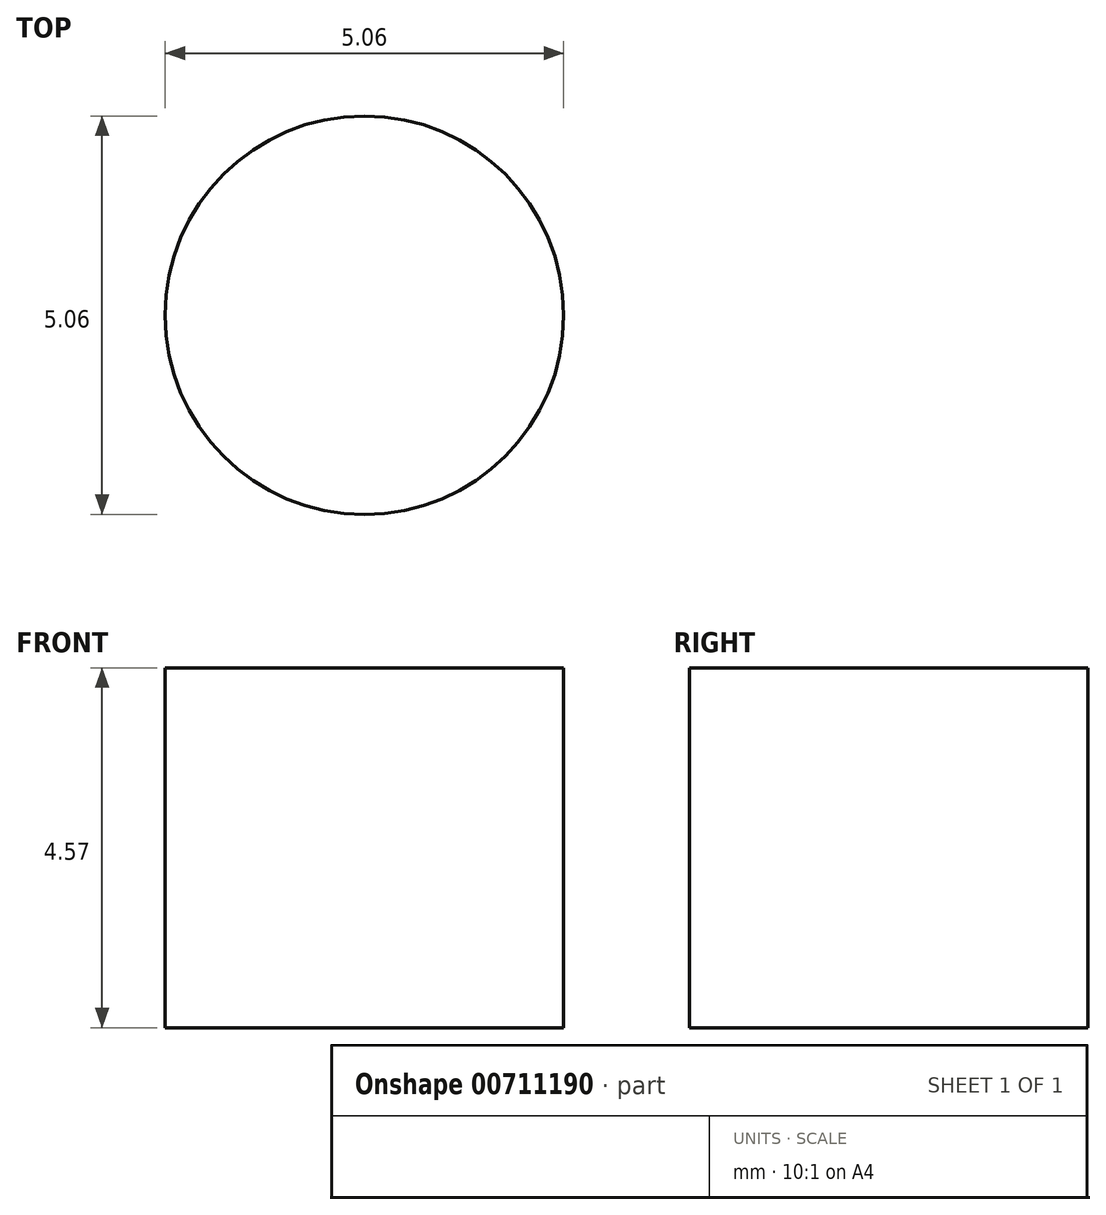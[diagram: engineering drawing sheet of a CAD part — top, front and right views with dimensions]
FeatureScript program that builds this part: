
annotation { "Feature Type Name" : "Feature", "Feature Type Description" : "" }
export const myFeature = defineFeature(function(context is Context, id is Id, definition is map)
    precondition{}
    {
        {
            var Q0;
            Q0=qCreatedBy(makeId("Top.planeOp"),FACE);
            var sketch = newSketch(context, id + "F0", { "sketchPlane" : qUnion([Q0])});
            skCircle(sketch, "E0", {"center": v(0.2, 0.2) * mm, "radius": 2.53 * mm});
            skSolve(sketch);
        }
        {
            var Q0;
            Q0=makeQuery(id+"F0.imprint","IMPRINT",FACE,{"disambiguationData":[TD([[makeQuery(id+"F0.imprint","IMPRINT",EDGE,{"derivedFrom":sQuery(id+"F0.wireOp",EDGE,"E0")}),1.0]])]});
            extrude(context, id + "F1", {"entities" : qUnion([Q0]), "depth" : 4.57 * mm, "offsetDistance" : 25.4 * mm});
        }
    });
